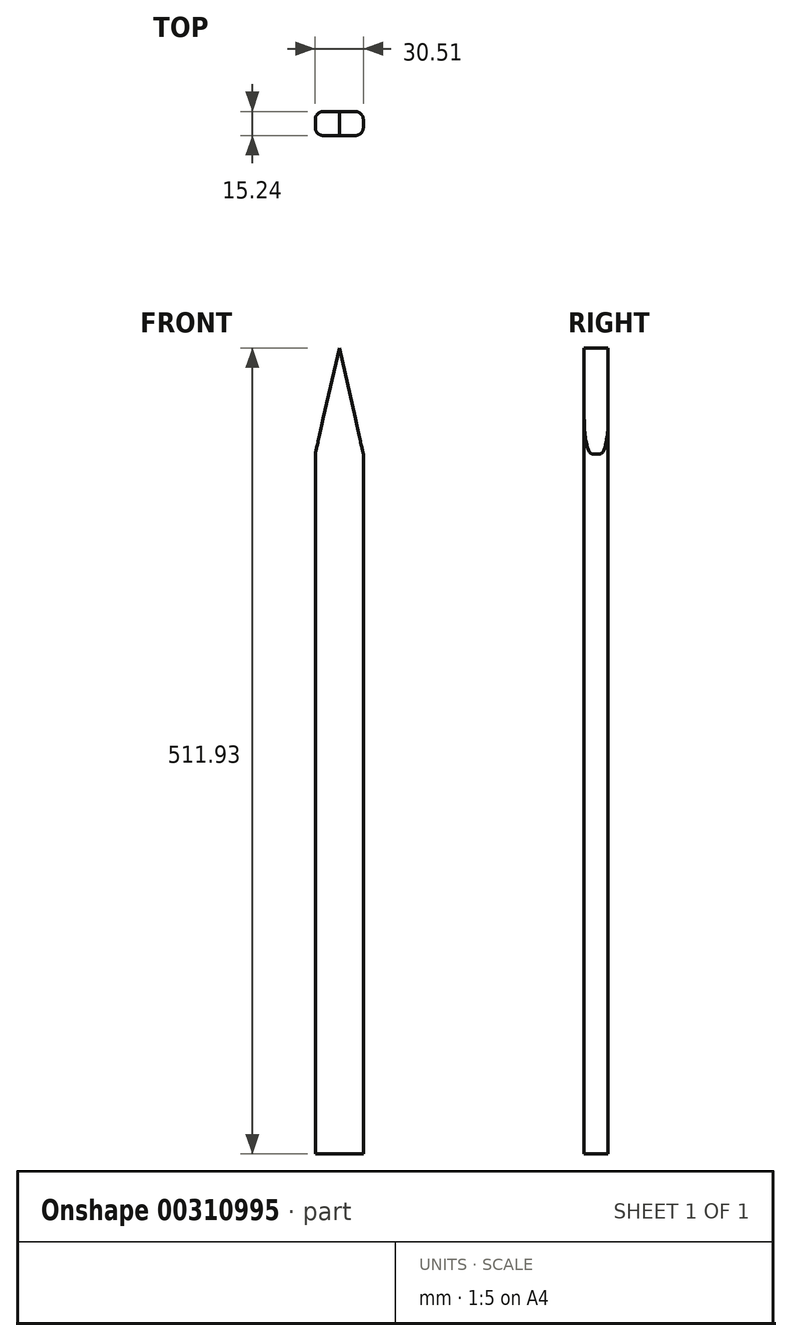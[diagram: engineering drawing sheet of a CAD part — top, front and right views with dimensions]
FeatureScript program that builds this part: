
annotation { "Feature Type Name" : "Feature", "Feature Type Description" : "" }
export const myFeature = defineFeature(function(context is Context, id is Id, definition is map)
    precondition{}
    {
        {
            var Q0;
            Q0=qCreatedBy(makeId("Front.planeOp"),FACE);
            var sketch = newSketch(context, id + "F0", { "sketchPlane" : qUnion([Q0])});
            skLineSegment(sketch, "E0", {"start": v(25.61, 71.95) * mm, "end": v(40.87, 139.17) * mm});
            skLineSegment(sketch, "E1", {"start": v(40.87, 139.17) * mm, "end": v(56.12, 71.95) * mm});
            skLineSegment(sketch, "E2", {"start": v(56.12, 71.95) * mm, "end": v(56.12, -372.76) * mm});
            skLineSegment(sketch, "E3", {"start": v(25.61, 71.95) * mm, "end": v(25.61, -372.76) * mm});
            skLineSegment(sketch, "E4", {"start": v(25.61, -372.76) * mm, "end": v(56.12, -372.76) * mm});
            skSolve(sketch);
        }
        {
            var Q0;
            Q0 = qSketchRegion(id + "F0", true);
            extrude(context, id + "F1", {"entities" : qUnion([Q0]), "depth" : 15.24 * mm});
        }
        {
            var Q0;
            Q0=makeQuery(id+"F1.opExtrude","CAP_EDGE",EDGE,{"disambiguationData":[OSD([sQuery(id+"F0.wireOp",EDGE,"E2")])],"isStart":false});
            var Q1;
            Q1=makeQuery(id+"F1.opExtrude","CAP_EDGE",EDGE,{"disambiguationData":[OSD([sQuery(id+"F0.wireOp",EDGE,"E3")])],"isStart":true});
            var Q2;
            Q2=makeQuery(id+"F1.opExtrude","CAP_EDGE",EDGE,{"disambiguationData":[OSD([sQuery(id+"F0.wireOp",EDGE,"E3")])],"isStart":false});
            var Q3;
            Q3=makeQuery(id+"F1.opExtrude","CAP_EDGE",EDGE,{"disambiguationData":[OSD([sQuery(id+"F0.wireOp",EDGE,"E2")])],"isStart":true});
            fillet(context, id + "F2", {"entities" : qUnion([Q0, Q1, Q2, Q3]), "radius" : 5.08 * mm, "tangentPropagation" : true, "allowEdgeOverflow" : false});
        }
    });
